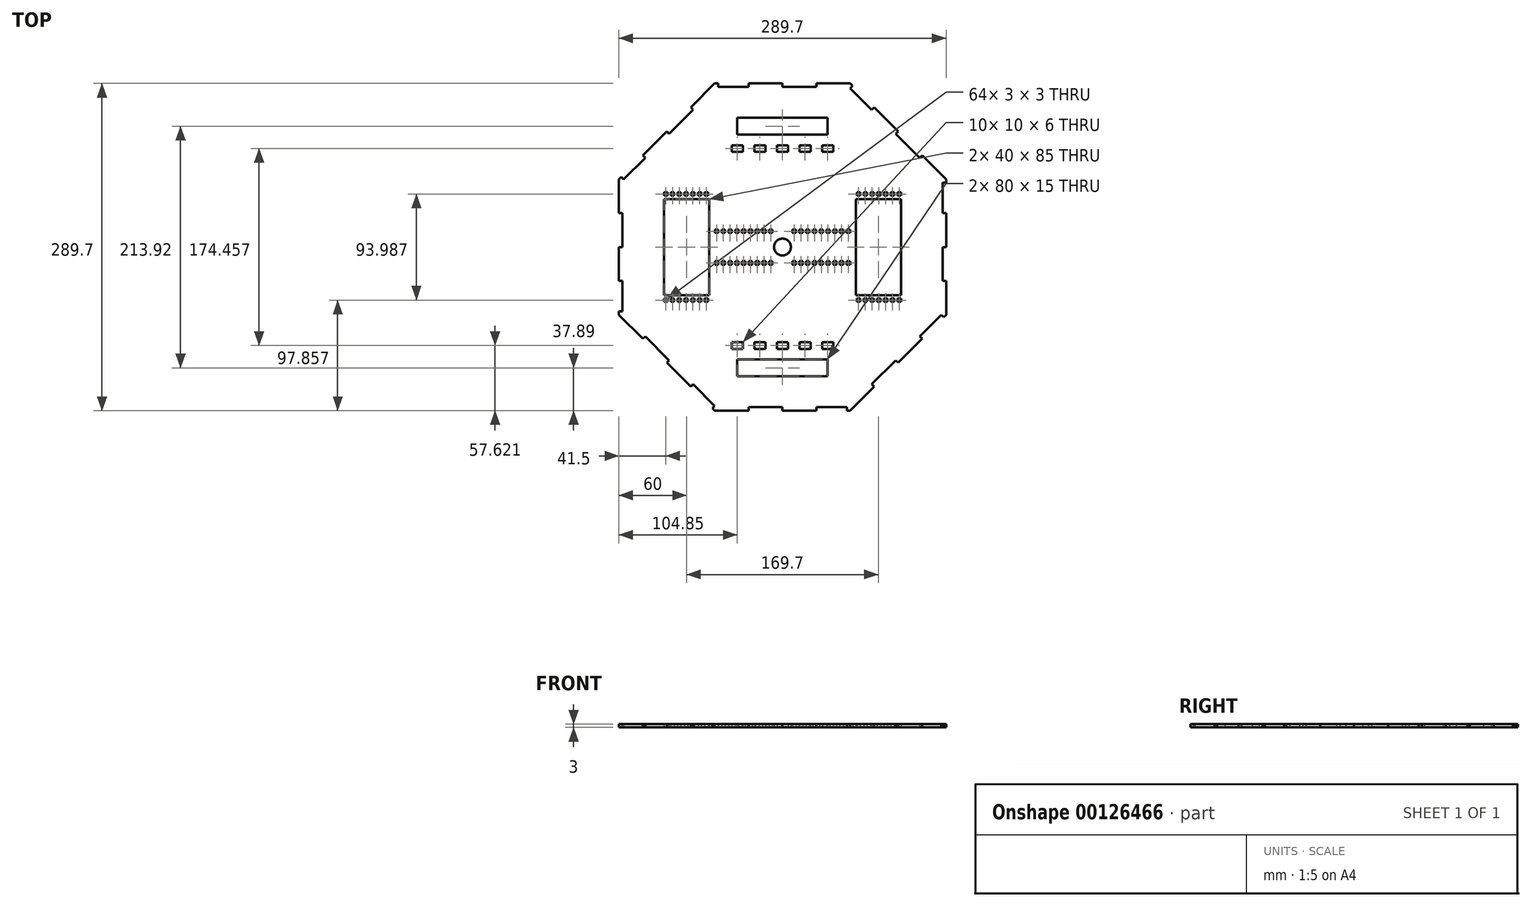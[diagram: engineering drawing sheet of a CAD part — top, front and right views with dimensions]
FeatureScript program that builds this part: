
annotation { "Feature Type Name" : "Feature", "Feature Type Description" : "" }
export const myFeature = defineFeature(function(context is Context, id is Id, definition is map)
    precondition{}
    {
        {
            var Q0;
            Q0=qCreatedBy(makeId("Top.planeOp"),FACE);
            var sketch = newSketch(context, id + "F0", { "sketchPlane" : qUnion([Q0])});
            skArc(sketch, "E0.cCircle", {"start": v(0, -144.85) * mm, "mid": v(14.74, 144.1) * mm, "end": v(-29.33, -141.85) * mm, "construction": true});
            skLineSegment(sketch, "E0.0", {"start": v(-60, 144.85) * mm, "end": v(-57, 144.85) * mm});
            skLineSegment(sketch, "E0.1", {"start": v(60, 144.85) * mm, "end": v(62.12, 142.73) * mm});
            skLineSegment(sketch, "E0.2", {"start": v(144.85, 60) * mm, "end": v(144.85, 57) * mm});
            skLineSegment(sketch, "E0.3", {"start": v(144.85, -60) * mm, "end": v(142.73, -62.12) * mm});
            skLineSegment(sketch, "E0.4", {"start": v(60, -144.85) * mm, "end": v(57, -144.85) * mm});
            skLineSegment(sketch, "E0.5", {"start": v(-60, -144.85) * mm, "end": v(-62.12, -142.73) * mm});
            skLineSegment(sketch, "E0.6", {"start": v(-144.85, -60) * mm, "end": v(-144.85, -57) * mm});
            skLineSegment(sketch, "E0.7", {"start": v(-144.85, 60) * mm, "end": v(-142.73, 62.12) * mm});
            skPoint(sketch, "E0.0.midPoint", {"position": v(0, 144.85) * mm});
            skLineSegment(sketch, "E1", {"start": v(144.85, 0) * mm, "end": v(-144.85, 0) * mm, "construction": true});
            skLineSegment(sketch, "E2", {"start": v(-144.85, 0) * mm, "end": v(-104.85, 0) * mm, "construction": true});
            skLineSegment(sketch, "E3", {"start": v(-104.85, 0) * mm, "end": v(-104.85, 42.5) * mm});
            skLineSegment(sketch, "E4", {"start": v(-104.85, 42.5) * mm, "end": v(-64.85, 42.5) * mm});
            skLineSegment(sketch, "E5", {"start": v(-64.85, 42.5) * mm, "end": v(-64.85, -42.5) * mm});
            skLineSegment(sketch, "E6", {"start": v(-64.85, -42.5) * mm, "end": v(-104.85, -42.5) * mm});
            skLineSegment(sketch, "E7", {"start": v(-104.85, -42.5) * mm, "end": v(-104.85, 0) * mm});
            skLineSegment(sketch, "E8", {"start": v(-64.85, 0) * mm, "end": v(-59.85, 0) * mm, "construction": true});
            skLineSegment(sketch, "E9", {"start": v(-59.85, 0) * mm, "end": v(-59.85, 15.5) * mm, "construction": true});
            skLineSegment(sketch, "E10", {"start": v(-59.85, 0) * mm, "end": v(-56.85, 0) * mm, "construction": true});
            skLineSegment(sketch, "E11", {"start": v(-56.85, 0) * mm, "end": v(-53.85, 0) * mm, "construction": true});
            skLineSegment(sketch, "E12", {"start": v(-53.85, 0) * mm, "end": v(-50.85, 0) * mm, "construction": true});
            skLineSegment(sketch, "E13", {"start": v(-50.85, 0) * mm, "end": v(-47.85, 0) * mm, "construction": true});
            skLineSegment(sketch, "E14", {"start": v(-47.85, 0) * mm, "end": v(-44.85, 0) * mm, "construction": true});
            skLineSegment(sketch, "E15", {"start": v(-44.85, 0) * mm, "end": v(-41.85, 0) * mm, "construction": true});
            skLineSegment(sketch, "E16", {"start": v(-41.85, 0) * mm, "end": v(-38.85, 0) * mm, "construction": true});
            skLineSegment(sketch, "E17", {"start": v(-38.85, 0) * mm, "end": v(-35.85, 0) * mm, "construction": true});
            skLineSegment(sketch, "E18", {"start": v(-35.85, 0) * mm, "end": v(-32.85, 0) * mm, "construction": true});
            skLineSegment(sketch, "E19", {"start": v(-32.85, 0) * mm, "end": v(-29.85, 0) * mm, "construction": true});
            skLineSegment(sketch, "E20", {"start": v(-29.85, 0) * mm, "end": v(-26.85, 0) * mm, "construction": true});
            skLineSegment(sketch, "E21", {"start": v(-26.85, 0) * mm, "end": v(-23.85, 0) * mm, "construction": true});
            skLineSegment(sketch, "E22", {"start": v(-23.85, 0) * mm, "end": v(-20.85, 0) * mm, "construction": true});
            skLineSegment(sketch, "E23", {"start": v(-20.85, 0) * mm, "end": v(-17.85, 0) * mm, "construction": true});
            skLineSegment(sketch, "E24", {"start": v(-17.85, 0) * mm, "end": v(-14.85, 0) * mm, "construction": true});
            skLineSegment(sketch, "E25", {"start": v(-14.85, 0) * mm, "end": v(-11.85, 0) * mm, "construction": true});
            skLineSegment(sketch, "E26", {"start": v(-59.85, 15.5) * mm, "end": v(-56.85, 15.5) * mm});
            skLineSegment(sketch, "E27", {"start": v(-56.85, 15.5) * mm, "end": v(-56.85, 12.5) * mm});
            skLineSegment(sketch, "E28", {"start": v(-56.85, 12.5) * mm, "end": v(-59.85, 12.5) * mm});
            skLineSegment(sketch, "E29", {"start": v(-59.85, 12.5) * mm, "end": v(-59.85, 15.5) * mm});
            skLineSegment(sketch, "E30", {"start": v(-53.85, 15.5) * mm, "end": v(-50.85, 15.5) * mm});
            skLineSegment(sketch, "E31", {"start": v(-50.85, 15.5) * mm, "end": v(-50.85, 12.5) * mm});
            skLineSegment(sketch, "E32", {"start": v(-50.85, 12.5) * mm, "end": v(-53.85, 12.5) * mm});
            skLineSegment(sketch, "E33", {"start": v(-59.85, 15.5) * mm, "end": v(-11.85, 15.5) * mm, "construction": true});
            skLineSegment(sketch, "E34", {"start": v(-47.85, 0) * mm, "end": v(-47.85, 15.5) * mm, "construction": true});
            skLineSegment(sketch, "E35", {"start": v(-41.85, 0) * mm, "end": v(-41.85, 15.5) * mm, "construction": true});
            skLineSegment(sketch, "E36", {"start": v(-35.85, 0) * mm, "end": v(-35.85, 15.5) * mm, "construction": true});
            skLineSegment(sketch, "E37", {"start": v(-29.85, 0) * mm, "end": v(-29.85, 15.5) * mm, "construction": true});
            skLineSegment(sketch, "E38", {"start": v(-23.85, 0) * mm, "end": v(-23.85, 15.5) * mm, "construction": true});
            skLineSegment(sketch, "E39", {"start": v(-17.85, 0) * mm, "end": v(-17.85, 15.5) * mm, "construction": true});
            skLineSegment(sketch, "E40", {"start": v(-53.85, 15.5) * mm, "end": v(-53.85, 12.5) * mm});
            skLineSegment(sketch, "E41", {"start": v(-47.85, 15.5) * mm, "end": v(-47.85, 12.5) * mm});
            skLineSegment(sketch, "E42", {"start": v(-47.85, 12.5) * mm, "end": v(-44.85, 12.5) * mm});
            skLineSegment(sketch, "E43", {"start": v(-44.85, 12.5) * mm, "end": v(-44.85, 15.5) * mm});
            skLineSegment(sketch, "E44", {"start": v(-44.85, 15.5) * mm, "end": v(-47.85, 15.5) * mm});
            skLineSegment(sketch, "E45", {"start": v(-41.85, 15.5) * mm, "end": v(-41.85, 12.5) * mm});
            skLineSegment(sketch, "E46", {"start": v(-41.85, 12.5) * mm, "end": v(-38.85, 12.5) * mm});
            skLineSegment(sketch, "E47", {"start": v(-38.85, 12.5) * mm, "end": v(-38.85, 15.5) * mm});
            skLineSegment(sketch, "E48", {"start": v(-38.85, 15.5) * mm, "end": v(-41.85, 15.5) * mm});
            skLineSegment(sketch, "E49", {"start": v(-35.85, 15.5) * mm, "end": v(-35.85, 12.5) * mm});
            skLineSegment(sketch, "E50", {"start": v(-35.85, 12.5) * mm, "end": v(-32.85, 12.5) * mm});
            skLineSegment(sketch, "E51", {"start": v(-32.85, 12.5) * mm, "end": v(-32.85, 15.5) * mm});
            skLineSegment(sketch, "E52", {"start": v(-32.85, 15.5) * mm, "end": v(-35.85, 15.5) * mm});
            skLineSegment(sketch, "E53", {"start": v(-29.85, 15.5) * mm, "end": v(-29.85, 12.5) * mm});
            skLineSegment(sketch, "E54", {"start": v(-29.85, 12.5) * mm, "end": v(-26.85, 12.5) * mm});
            skLineSegment(sketch, "E55", {"start": v(-26.85, 12.5) * mm, "end": v(-26.85, 15.5) * mm});
            skLineSegment(sketch, "E56", {"start": v(-26.85, 15.5) * mm, "end": v(-29.85, 15.5) * mm});
            skLineSegment(sketch, "E57", {"start": v(-23.85, 15.5) * mm, "end": v(-23.85, 12.5) * mm});
            skLineSegment(sketch, "E58", {"start": v(-23.85, 12.5) * mm, "end": v(-20.85, 12.5) * mm});
            skLineSegment(sketch, "E59", {"start": v(-20.85, 12.5) * mm, "end": v(-20.85, 15.5) * mm});
            skLineSegment(sketch, "E60", {"start": v(-20.85, 15.5) * mm, "end": v(-23.85, 15.5) * mm});
            skLineSegment(sketch, "E61", {"start": v(-17.85, 15.5) * mm, "end": v(-17.85, 12.5) * mm});
            skLineSegment(sketch, "E62", {"start": v(-17.85, 12.5) * mm, "end": v(-14.85, 12.5) * mm});
            skLineSegment(sketch, "E63", {"start": v(-14.85, 12.5) * mm, "end": v(-14.85, 15.5) * mm});
            skLineSegment(sketch, "E64", {"start": v(-14.85, 15.5) * mm, "end": v(-17.85, 15.5) * mm});
            skLineSegment(sketch, "E65", {"start": v(-11.85, 15.5) * mm, "end": v(-11.85, 12.5) * mm});
            skLineSegment(sketch, "E66", {"start": v(-11.85, 12.5) * mm, "end": v(-8.85, 12.5) * mm});
            skLineSegment(sketch, "E67", {"start": v(-8.85, 12.5) * mm, "end": v(-8.85, 15.5) * mm});
            skLineSegment(sketch, "E68", {"start": v(-8.85, 15.5) * mm, "end": v(-11.85, 15.5) * mm});
            skLineSegment(sketch, "E69.MirrorCS", {"start": v(-47.85, -15.5) * mm, "end": v(-47.85, -12.5) * mm});
            skLineSegment(sketch, "E70.MirrorCS", {"start": v(-50.85, -12.5) * mm, "end": v(-53.85, -12.5) * mm});
            skLineSegment(sketch, "E71.MirrorCS", {"start": v(-53.85, -15.5) * mm, "end": v(-53.85, -12.5) * mm});
            skLineSegment(sketch, "E72.MirrorCS", {"start": v(-50.85, -15.5) * mm, "end": v(-50.85, -12.5) * mm});
            skLineSegment(sketch, "E73.MirrorCS", {"start": v(-41.85, -15.5) * mm, "end": v(-41.85, -12.5) * mm});
            skLineSegment(sketch, "E74.MirrorCS", {"start": v(-47.85, -12.5) * mm, "end": v(-44.85, -12.5) * mm});
            skLineSegment(sketch, "E75.MirrorCS", {"start": v(-59.85, -15.5) * mm, "end": v(-56.85, -15.5) * mm});
            skLineSegment(sketch, "E76.MirrorCS", {"start": v(-44.85, -12.5) * mm, "end": v(-44.85, -15.5) * mm});
            skLineSegment(sketch, "E77.MirrorCS", {"start": v(-32.85, -15.5) * mm, "end": v(-35.85, -15.5) * mm});
            skLineSegment(sketch, "E78.MirrorCS", {"start": v(-41.85, -12.5) * mm, "end": v(-38.85, -12.5) * mm});
            skLineSegment(sketch, "E79.MirrorCS", {"start": v(-53.85, -15.5) * mm, "end": v(-50.85, -15.5) * mm});
            skLineSegment(sketch, "E80.MirrorCS", {"start": v(-23.85, -15.5) * mm, "end": v(-23.85, -12.5) * mm});
            skLineSegment(sketch, "E81.MirrorCS", {"start": v(-14.85, -15.5) * mm, "end": v(-17.85, -15.5) * mm});
            skLineSegment(sketch, "E82.MirrorCS", {"start": v(-38.85, -15.5) * mm, "end": v(-41.85, -15.5) * mm});
            skLineSegment(sketch, "E83.MirrorCS", {"start": v(-35.85, -15.5) * mm, "end": v(-35.85, -12.5) * mm});
            skLineSegment(sketch, "E84.MirrorCS", {"start": v(-59.85, -15.5) * mm, "end": v(-11.85, -15.5) * mm, "construction": true});
            skLineSegment(sketch, "E85.MirrorCS", {"start": v(-26.85, -15.5) * mm, "end": v(-29.85, -15.5) * mm});
            skLineSegment(sketch, "E86.MirrorCS", {"start": v(-11.85, -15.5) * mm, "end": v(-11.85, -12.5) * mm});
            skLineSegment(sketch, "E87.MirrorCS", {"start": v(-14.85, -12.5) * mm, "end": v(-14.85, -15.5) * mm});
            skLineSegment(sketch, "E88.MirrorCS", {"start": v(-38.85, -12.5) * mm, "end": v(-38.85, -15.5) * mm});
            skLineSegment(sketch, "E89.MirrorCS", {"start": v(-29.85, -12.5) * mm, "end": v(-26.85, -12.5) * mm});
            skLineSegment(sketch, "E90.MirrorCS", {"start": v(-23.85, -12.5) * mm, "end": v(-20.85, -12.5) * mm});
            skLineSegment(sketch, "E91.MirrorCS", {"start": v(-56.85, -12.5) * mm, "end": v(-59.85, -12.5) * mm});
            skLineSegment(sketch, "E92.MirrorCS", {"start": v(-17.85, -15.5) * mm, "end": v(-17.85, -12.5) * mm});
            skLineSegment(sketch, "E93.MirrorCS", {"start": v(-44.85, -15.5) * mm, "end": v(-47.85, -15.5) * mm});
            skLineSegment(sketch, "E94.MirrorCS", {"start": v(-59.85, -12.5) * mm, "end": v(-59.85, -15.5) * mm});
            skLineSegment(sketch, "E95.MirrorCS", {"start": v(-8.85, -15.5) * mm, "end": v(-11.85, -15.5) * mm});
            skLineSegment(sketch, "E96.MirrorCS", {"start": v(-20.85, -12.5) * mm, "end": v(-20.85, -15.5) * mm});
            skLineSegment(sketch, "E97.MirrorCS", {"start": v(-56.85, -15.5) * mm, "end": v(-56.85, -12.5) * mm});
            skLineSegment(sketch, "E98.MirrorCS", {"start": v(-17.85, -12.5) * mm, "end": v(-14.85, -12.5) * mm});
            skLineSegment(sketch, "E99.MirrorCS", {"start": v(-32.85, -12.5) * mm, "end": v(-32.85, -15.5) * mm});
            skLineSegment(sketch, "E100.MirrorCS", {"start": v(-26.85, -12.5) * mm, "end": v(-26.85, -15.5) * mm});
            skLineSegment(sketch, "E101.MirrorCS", {"start": v(-8.85, -12.5) * mm, "end": v(-8.85, -15.5) * mm});
            skLineSegment(sketch, "E102.MirrorCS", {"start": v(-11.85, -12.5) * mm, "end": v(-8.85, -12.5) * mm});
            skLineSegment(sketch, "E103.MirrorCS", {"start": v(-35.85, -12.5) * mm, "end": v(-32.85, -12.5) * mm});
            skLineSegment(sketch, "E104.MirrorCS", {"start": v(-20.85, -15.5) * mm, "end": v(-23.85, -15.5) * mm});
            skLineSegment(sketch, "E105.MirrorCS", {"start": v(-29.85, -15.5) * mm, "end": v(-29.85, -12.5) * mm});
            skLineSegment(sketch, "E106.MirrorCS", {"start": v(-59.85, 0) * mm, "end": v(-59.85, -15.5) * mm, "construction": true});
            skLineSegment(sketch, "E107.MirrorCS", {"start": v(-17.85, 0) * mm, "end": v(-17.85, -15.5) * mm, "construction": true});
            skLineSegment(sketch, "E108.MirrorCS", {"start": v(-29.85, 0) * mm, "end": v(-29.85, -15.5) * mm, "construction": true});
            skLineSegment(sketch, "E109.MirrorCS", {"start": v(-23.85, 0) * mm, "end": v(-23.85, -15.5) * mm, "construction": true});
            skLineSegment(sketch, "E110.MirrorCS", {"start": v(-35.85, 0) * mm, "end": v(-35.85, -15.5) * mm, "construction": true});
            skLineSegment(sketch, "E111.MirrorCS", {"start": v(-41.85, 0) * mm, "end": v(-41.85, -15.5) * mm, "construction": true});
            skLineSegment(sketch, "E112.MirrorCS", {"start": v(-47.85, 0) * mm, "end": v(-47.85, -15.5) * mm, "construction": true});
            skLineSegment(sketch, "E113.MirrorCS", {"start": v(26.85, 12.5) * mm, "end": v(26.85, 15.5) * mm});
            skLineSegment(sketch, "E114.MirrorCS", {"start": v(23.85, 12.5) * mm, "end": v(20.85, 12.5) * mm});
            skLineSegment(sketch, "E115.MirrorCS", {"start": v(26.85, 15.5) * mm, "end": v(29.85, 15.5) * mm});
            skLineSegment(sketch, "E116.MirrorCS", {"start": v(20.85, 12.5) * mm, "end": v(20.85, 15.5) * mm});
            skLineSegment(sketch, "E117.MirrorCS", {"start": v(23.85, 15.5) * mm, "end": v(23.85, 12.5) * mm});
            skLineSegment(sketch, "E118.MirrorCS", {"start": v(20.85, 15.5) * mm, "end": v(23.85, 15.5) * mm});
            skLineSegment(sketch, "E119.MirrorCS", {"start": v(17.85, 15.5) * mm, "end": v(17.85, 12.5) * mm});
            skLineSegment(sketch, "E120.MirrorCS", {"start": v(32.85, 15.5) * mm, "end": v(35.85, 15.5) * mm});
            skLineSegment(sketch, "E121.MirrorCS", {"start": v(35.85, 15.5) * mm, "end": v(35.85, 12.5) * mm});
            skLineSegment(sketch, "E122.MirrorCS", {"start": v(38.85, 0) * mm, "end": v(35.85, 0) * mm, "construction": true});
            skLineSegment(sketch, "E123.MirrorCS", {"start": v(32.85, 12.5) * mm, "end": v(32.85, 15.5) * mm});
            skLineSegment(sketch, "E124.MirrorCS", {"start": v(32.85, 0) * mm, "end": v(29.85, 0) * mm, "construction": true});
            skLineSegment(sketch, "E125.MirrorCS", {"start": v(35.85, 0) * mm, "end": v(32.85, 0) * mm, "construction": true});
            skLineSegment(sketch, "E126.MirrorCS", {"start": v(29.85, 12.5) * mm, "end": v(26.85, 12.5) * mm});
            skLineSegment(sketch, "E127.MirrorCS", {"start": v(29.85, 15.5) * mm, "end": v(29.85, 12.5) * mm});
            skLineSegment(sketch, "E128.MirrorCS", {"start": v(35.85, 12.5) * mm, "end": v(32.85, 12.5) * mm});
            skLineSegment(sketch, "E129.MirrorCS", {"start": v(47.85, 12.5) * mm, "end": v(44.85, 12.5) * mm});
            skLineSegment(sketch, "E130.MirrorCS", {"start": v(44.85, 12.5) * mm, "end": v(44.85, 15.5) * mm});
            skLineSegment(sketch, "E131.MirrorCS", {"start": v(47.85, 15.5) * mm, "end": v(47.85, 12.5) * mm});
            skLineSegment(sketch, "E132.MirrorCS", {"start": v(44.85, 15.5) * mm, "end": v(47.85, 15.5) * mm});
            skLineSegment(sketch, "E133.MirrorCS", {"start": v(41.85, 15.5) * mm, "end": v(41.85, 12.5) * mm});
            skLineSegment(sketch, "E134.MirrorCS", {"start": v(41.85, 12.5) * mm, "end": v(38.85, 12.5) * mm});
            skLineSegment(sketch, "E135.MirrorCS", {"start": v(53.85, 15.5) * mm, "end": v(50.85, 15.5) * mm});
            skLineSegment(sketch, "E136.MirrorCS", {"start": v(41.85, -12.5) * mm, "end": v(38.85, -12.5) * mm});
            skLineSegment(sketch, "E137.MirrorCS", {"start": v(17.85, 12.5) * mm, "end": v(14.85, 12.5) * mm});
            skLineSegment(sketch, "E138.MirrorCS", {"start": v(38.85, 12.5) * mm, "end": v(38.85, 15.5) * mm});
            skLineSegment(sketch, "E139.MirrorCS", {"start": v(50.85, 15.5) * mm, "end": v(50.85, 12.5) * mm});
            skLineSegment(sketch, "E140.MirrorCS", {"start": v(38.85, 15.5) * mm, "end": v(41.85, 15.5) * mm});
            skLineSegment(sketch, "E141.MirrorCS", {"start": v(50.85, 12.5) * mm, "end": v(53.85, 12.5) * mm});
            skLineSegment(sketch, "E142.MirrorCS", {"start": v(29.85, 0) * mm, "end": v(26.85, 0) * mm, "construction": true});
            skLineSegment(sketch, "E143.MirrorCS", {"start": v(35.85, 0) * mm, "end": v(35.85, 15.5) * mm, "construction": true});
            skLineSegment(sketch, "E144.MirrorCS", {"start": v(38.85, -15.5) * mm, "end": v(41.85, -15.5) * mm});
            skLineSegment(sketch, "E145.MirrorCS", {"start": v(29.85, 0) * mm, "end": v(29.85, 15.5) * mm, "construction": true});
            skLineSegment(sketch, "E146.MirrorCS", {"start": v(26.85, 0) * mm, "end": v(23.85, 0) * mm, "construction": true});
            skLineSegment(sketch, "E147.MirrorCS", {"start": v(47.85, -12.5) * mm, "end": v(44.85, -12.5) * mm});
            skLineSegment(sketch, "E148.MirrorCS", {"start": v(59.85, 15.5) * mm, "end": v(56.85, 15.5) * mm});
            skLineSegment(sketch, "E149.MirrorCS", {"start": v(23.85, -12.5) * mm, "end": v(20.85, -12.5) * mm});
            skLineSegment(sketch, "E150.MirrorCS", {"start": v(38.85, -12.5) * mm, "end": v(38.85, -15.5) * mm});
            skLineSegment(sketch, "E151.MirrorCS", {"start": v(41.85, -15.5) * mm, "end": v(41.85, -12.5) * mm});
            skLineSegment(sketch, "E152.MirrorCS", {"start": v(53.85, 0) * mm, "end": v(50.85, 0) * mm, "construction": true});
            skLineSegment(sketch, "E153.MirrorCS", {"start": v(17.85, -15.5) * mm, "end": v(17.85, -12.5) * mm});
            skLineSegment(sketch, "E154.MirrorCS", {"start": v(50.85, 0) * mm, "end": v(47.85, 0) * mm, "construction": true});
            skLineSegment(sketch, "E155.MirrorCS", {"start": v(32.85, -15.5) * mm, "end": v(35.85, -15.5) * mm});
            skLineSegment(sketch, "E156.MirrorCS", {"start": v(47.85, 0) * mm, "end": v(44.85, 0) * mm, "construction": true});
            skLineSegment(sketch, "E157.MirrorCS", {"start": v(44.85, 0) * mm, "end": v(41.85, 0) * mm, "construction": true});
            skLineSegment(sketch, "E158.MirrorCS", {"start": v(14.85, 12.5) * mm, "end": v(14.85, 15.5) * mm});
            skLineSegment(sketch, "E159.MirrorCS", {"start": v(41.85, 0) * mm, "end": v(38.85, 0) * mm, "construction": true});
            skLineSegment(sketch, "E160.MirrorCS", {"start": v(20.85, -12.5) * mm, "end": v(20.85, -15.5) * mm});
            skLineSegment(sketch, "E161.MirrorCS", {"start": v(14.85, 15.5) * mm, "end": v(17.85, 15.5) * mm});
            skLineSegment(sketch, "E162.MirrorCS", {"start": v(14.85, -12.5) * mm, "end": v(14.85, -15.5) * mm});
            skLineSegment(sketch, "E163.MirrorCS", {"start": v(17.85, -12.5) * mm, "end": v(14.85, -12.5) * mm});
            skLineSegment(sketch, "E164.MirrorCS", {"start": v(14.85, -15.5) * mm, "end": v(17.85, -15.5) * mm});
            skLineSegment(sketch, "E165.MirrorCS", {"start": v(11.85, 15.5) * mm, "end": v(11.85, 12.5) * mm});
            skLineSegment(sketch, "E166.MirrorCS", {"start": v(35.85, -15.5) * mm, "end": v(35.85, -12.5) * mm});
            skLineSegment(sketch, "E167.MirrorCS", {"start": v(47.85, 0) * mm, "end": v(47.85, 15.5) * mm, "construction": true});
            skLineSegment(sketch, "E168.MirrorCS", {"start": v(17.85, 0) * mm, "end": v(17.85, 15.5) * mm, "construction": true});
            skLineSegment(sketch, "E169.MirrorCS", {"start": v(20.85, 0) * mm, "end": v(17.85, 0) * mm, "construction": true});
            skLineSegment(sketch, "E170.MirrorCS", {"start": v(59.85, 0) * mm, "end": v(56.85, 0) * mm, "construction": true});
            skLineSegment(sketch, "E171.MirrorCS", {"start": v(64.85, 0) * mm, "end": v(59.85, 0) * mm, "construction": true});
            skLineSegment(sketch, "E172.MirrorCS", {"start": v(53.85, 15.5) * mm, "end": v(53.85, 12.5) * mm});
            skLineSegment(sketch, "E173.MirrorCS", {"start": v(17.85, 0) * mm, "end": v(14.85, 0) * mm, "construction": true});
            skLineSegment(sketch, "E174.MirrorCS", {"start": v(20.85, -15.5) * mm, "end": v(23.85, -15.5) * mm});
            skLineSegment(sketch, "E175.MirrorCS", {"start": v(56.85, 0) * mm, "end": v(53.85, 0) * mm, "construction": true});
            skLineSegment(sketch, "E176.MirrorCS", {"start": v(59.85, -15.5) * mm, "end": v(56.85, -15.5) * mm});
            skLineSegment(sketch, "E177.MirrorCS", {"start": v(56.85, 15.5) * mm, "end": v(56.85, 12.5) * mm});
            skLineSegment(sketch, "E178.MirrorCS", {"start": v(56.85, -12.5) * mm, "end": v(59.85, -12.5) * mm});
            skLineSegment(sketch, "E179.MirrorCS", {"start": v(59.85, 0) * mm, "end": v(59.85, 15.5) * mm, "construction": true});
            skLineSegment(sketch, "E180.MirrorCS", {"start": v(14.85, 0) * mm, "end": v(11.85, 0) * mm, "construction": true});
            skLineSegment(sketch, "E181.MirrorCS", {"start": v(29.85, -15.5) * mm, "end": v(29.85, -12.5) * mm});
            skLineSegment(sketch, "E182.MirrorCS", {"start": v(29.85, -12.5) * mm, "end": v(26.85, -12.5) * mm});
            skLineSegment(sketch, "E183.MirrorCS", {"start": v(44.85, -12.5) * mm, "end": v(44.85, -15.5) * mm});
            skLineSegment(sketch, "E184.MirrorCS", {"start": v(56.85, 12.5) * mm, "end": v(59.85, 12.5) * mm});
            skLineSegment(sketch, "E185.MirrorCS", {"start": v(59.85, 12.5) * mm, "end": v(59.85, 15.5) * mm});
            skLineSegment(sketch, "E186.MirrorCS", {"start": v(44.85, -15.5) * mm, "end": v(47.85, -15.5) * mm});
            skLineSegment(sketch, "E187.MirrorCS", {"start": v(53.85, -15.5) * mm, "end": v(50.85, -15.5) * mm});
            skLineSegment(sketch, "E188.MirrorCS", {"start": v(23.85, -15.5) * mm, "end": v(23.85, -12.5) * mm});
            skLineSegment(sketch, "E189.MirrorCS", {"start": v(26.85, -12.5) * mm, "end": v(26.85, -15.5) * mm});
            skLineSegment(sketch, "E190.MirrorCS", {"start": v(35.85, -12.5) * mm, "end": v(32.85, -12.5) * mm});
            skLineSegment(sketch, "E191.MirrorCS", {"start": v(8.85, 15.5) * mm, "end": v(11.85, 15.5) * mm});
            skLineSegment(sketch, "E192.MirrorCS", {"start": v(11.85, 12.5) * mm, "end": v(8.85, 12.5) * mm});
            skLineSegment(sketch, "E193.MirrorCS", {"start": v(59.85, 15.5) * mm, "end": v(11.85, 15.5) * mm, "construction": true});
            skLineSegment(sketch, "E194.MirrorCS", {"start": v(41.85, 0) * mm, "end": v(41.85, 15.5) * mm, "construction": true});
            skLineSegment(sketch, "E195.MirrorCS", {"start": v(32.85, -12.5) * mm, "end": v(32.85, -15.5) * mm});
            skLineSegment(sketch, "E196.MirrorCS", {"start": v(8.85, 12.5) * mm, "end": v(8.85, 15.5) * mm});
            skLineSegment(sketch, "E197.MirrorCS", {"start": v(47.85, -15.5) * mm, "end": v(47.85, -12.5) * mm});
            skLineSegment(sketch, "E198.MirrorCS", {"start": v(50.85, -12.5) * mm, "end": v(53.85, -12.5) * mm});
            skLineSegment(sketch, "E199.MirrorCS", {"start": v(23.85, 0) * mm, "end": v(23.85, 15.5) * mm, "construction": true});
            skLineSegment(sketch, "E200.MirrorCS", {"start": v(26.85, -15.5) * mm, "end": v(29.85, -15.5) * mm});
            skLineSegment(sketch, "E201.MirrorCS", {"start": v(23.85, 0) * mm, "end": v(20.85, 0) * mm, "construction": true});
            skLineSegment(sketch, "E202.MirrorCS", {"start": v(53.85, -15.5) * mm, "end": v(53.85, -12.5) * mm});
            skLineSegment(sketch, "E203.MirrorCS", {"start": v(50.85, -15.5) * mm, "end": v(50.85, -12.5) * mm});
            skLineSegment(sketch, "E204.MirrorCS", {"start": v(59.85, -12.5) * mm, "end": v(59.85, -15.5) * mm});
            skLineSegment(sketch, "E205.MirrorCS", {"start": v(59.85, -15.5) * mm, "end": v(11.85, -15.5) * mm, "construction": true});
            skLineSegment(sketch, "E206.MirrorCS", {"start": v(56.85, -15.5) * mm, "end": v(56.85, -12.5) * mm});
            skLineSegment(sketch, "E207.MirrorCS", {"start": v(8.85, -15.5) * mm, "end": v(11.85, -15.5) * mm});
            skLineSegment(sketch, "E208.MirrorCS", {"start": v(11.85, -12.5) * mm, "end": v(8.85, -12.5) * mm});
            skLineSegment(sketch, "E209.MirrorCS", {"start": v(11.85, -15.5) * mm, "end": v(11.85, -12.5) * mm});
            skLineSegment(sketch, "E210.MirrorCS", {"start": v(8.85, -12.5) * mm, "end": v(8.85, -15.5) * mm});
            skLineSegment(sketch, "E211.MirrorCS", {"start": v(104.85, -42.5) * mm, "end": v(104.85, 0) * mm});
            skLineSegment(sketch, "E212.MirrorCS", {"start": v(59.85, 0) * mm, "end": v(59.85, -15.5) * mm, "construction": true});
            skLineSegment(sketch, "E213.MirrorCS", {"start": v(17.85, 0) * mm, "end": v(17.85, -15.5) * mm, "construction": true});
            skLineSegment(sketch, "E214.MirrorCS", {"start": v(29.85, 0) * mm, "end": v(29.85, -15.5) * mm, "construction": true});
            skLineSegment(sketch, "E215.MirrorCS", {"start": v(23.85, 0) * mm, "end": v(23.85, -15.5) * mm, "construction": true});
            skLineSegment(sketch, "E216.MirrorCS", {"start": v(35.85, 0) * mm, "end": v(35.85, -15.5) * mm, "construction": true});
            skLineSegment(sketch, "E217.MirrorCS", {"start": v(41.85, 0) * mm, "end": v(41.85, -15.5) * mm, "construction": true});
            skLineSegment(sketch, "E218.MirrorCS", {"start": v(47.85, 0) * mm, "end": v(47.85, -15.5) * mm, "construction": true});
            skLineSegment(sketch, "E219.MirrorCS", {"start": v(104.85, 0) * mm, "end": v(104.85, 42.5) * mm});
            skLineSegment(sketch, "E220.MirrorCS", {"start": v(64.85, -42.5) * mm, "end": v(104.85, -42.5) * mm});
            skLineSegment(sketch, "E221.MirrorCS", {"start": v(64.85, 42.5) * mm, "end": v(64.85, -42.5) * mm});
            skLineSegment(sketch, "E222.MirrorCS", {"start": v(104.85, 42.5) * mm, "end": v(64.85, 42.5) * mm});
            skCircle(sketch, "E223.MirrorC", {"center": v(0, 0) * mm, "radius": 144.85 * mm, "construction": true});
            skLineSegment(sketch, "E224", {"start": v(-60, -144.85) * mm, "end": v(-30, -144.85) * mm});
            skLineSegment(sketch, "E225", {"start": v(-30, -144.85) * mm, "end": v(-30, -141.85) * mm});
            skLineSegment(sketch, "E226", {"start": v(-30, -141.85) * mm, "end": v(0, -141.85) * mm});
            skLineSegment(sketch, "E227", {"start": v(0, -141.85) * mm, "end": v(0, -144.85) * mm});
            skLineSegment(sketch, "E228", {"start": v(0, -144.85) * mm, "end": v(30, -144.85) * mm});
            skLineSegment(sketch, "E229", {"start": v(30, -144.85) * mm, "end": v(30, -141.85) * mm});
            skLineSegment(sketch, "E230", {"start": v(60, -144.85) * mm, "end": v(0, -84.85) * mm, "construction": true});
            skLineSegment(sketch, "E231", {"start": v(0, -84.85) * mm, "end": v(-60, -144.85) * mm, "construction": true});
            skLineSegment(sketch, "E232", {"start": v(30, -141.85) * mm, "end": v(57, -141.85) * mm});
            skLineSegment(sketch, "E233", {"start": v(57, -141.85) * mm, "end": v(57, -144.85) * mm});
            skLineSegment(sketch, "E234.trimOffspring", {"start": v(-30, -144.85) * mm, "end": v(-60, -144.85) * mm});
            skLineSegment(sketch, "E235.trimOffspring", {"start": v(30, -144.85) * mm, "end": v(0, -144.85) * mm});
            skLineSegment(sketch, "E236", {"start": v(60, -144.85) * mm, "end": v(81.21, -123.64) * mm});
            skLineSegment(sketch, "E237", {"start": v(81.21, -123.64) * mm, "end": v(79.1, -121.52) * mm});
            skLineSegment(sketch, "E238", {"start": v(79.1, -121.52) * mm, "end": v(100.3, -100.3) * mm});
            skLineSegment(sketch, "E239", {"start": v(100.3, -100.3) * mm, "end": v(102.43, -102.42) * mm});
            skLineSegment(sketch, "E240", {"start": v(102.43, -102.42) * mm, "end": v(123.64, -81.21) * mm});
            skLineSegment(sketch, "E241", {"start": v(123.64, -81.21) * mm, "end": v(121.52, -79.09) * mm});
            skLineSegment(sketch, "E242", {"start": v(121.52, -79.09) * mm, "end": v(140.6, -60) * mm});
            skLineSegment(sketch, "E243", {"start": v(140.6, -60) * mm, "end": v(142.73, -62.12) * mm});
            skLineSegment(sketch, "E244", {"start": v(144.85, -60) * mm, "end": v(144.85, -30) * mm});
            skLineSegment(sketch, "E245", {"start": v(144.85, -30) * mm, "end": v(141.85, -30) * mm});
            skLineSegment(sketch, "E246", {"start": v(141.85, -30) * mm, "end": v(141.85, 0) * mm});
            skLineSegment(sketch, "E247", {"start": v(141.85, 0) * mm, "end": v(144.85, 0) * mm});
            skLineSegment(sketch, "E248", {"start": v(144.85, 0) * mm, "end": v(144.85, 30) * mm});
            skLineSegment(sketch, "E249", {"start": v(144.85, 30) * mm, "end": v(141.85, 30) * mm});
            skLineSegment(sketch, "E250", {"start": v(141.85, 30) * mm, "end": v(141.85, 57) * mm});
            skLineSegment(sketch, "E251", {"start": v(141.85, 57) * mm, "end": v(144.85, 57) * mm});
            skLineSegment(sketch, "E252", {"start": v(144.85, 60) * mm, "end": v(123.64, 81.21) * mm});
            skLineSegment(sketch, "E253", {"start": v(123.64, 81.21) * mm, "end": v(121.52, 79.1) * mm});
            skLineSegment(sketch, "E254", {"start": v(121.52, 79.1) * mm, "end": v(100.3, 100.3) * mm});
            skLineSegment(sketch, "E255", {"start": v(100.3, 100.3) * mm, "end": v(102.42, 102.43) * mm});
            skLineSegment(sketch, "E256", {"start": v(102.42, 102.43) * mm, "end": v(81.21, 123.64) * mm});
            skLineSegment(sketch, "E257", {"start": v(81.21, 123.64) * mm, "end": v(79.09, 121.52) * mm});
            skLineSegment(sketch, "E258", {"start": v(79.09, 121.52) * mm, "end": v(60, 140.6) * mm});
            skLineSegment(sketch, "E259", {"start": v(60, 140.6) * mm, "end": v(62.12, 142.73) * mm});
            skLineSegment(sketch, "E260", {"start": v(60, 144.85) * mm, "end": v(30, 144.85) * mm});
            skLineSegment(sketch, "E261", {"start": v(30, 144.85) * mm, "end": v(30, 141.85) * mm});
            skLineSegment(sketch, "E262", {"start": v(30, 141.85) * mm, "end": v(0, 141.85) * mm});
            skLineSegment(sketch, "E263", {"start": v(0, 141.85) * mm, "end": v(0, 144.85) * mm});
            skLineSegment(sketch, "E264", {"start": v(0, 144.85) * mm, "end": v(-30, 144.85) * mm});
            skLineSegment(sketch, "E265", {"start": v(-30, 144.85) * mm, "end": v(-30, 141.85) * mm});
            skLineSegment(sketch, "E266", {"start": v(-30, 141.85) * mm, "end": v(-57, 141.85) * mm});
            skLineSegment(sketch, "E267", {"start": v(-57, 141.85) * mm, "end": v(-57, 144.85) * mm});
            skLineSegment(sketch, "E268", {"start": v(-60, 144.85) * mm, "end": v(-81.21, 123.64) * mm});
            skLineSegment(sketch, "E269", {"start": v(-81.21, 123.64) * mm, "end": v(-79.1, 121.52) * mm});
            skLineSegment(sketch, "E270", {"start": v(-79.1, 121.52) * mm, "end": v(-100.3, 100.3) * mm});
            skLineSegment(sketch, "E271", {"start": v(-100.3, 100.3) * mm, "end": v(-102.43, 102.42) * mm});
            skLineSegment(sketch, "E272", {"start": v(-102.43, 102.42) * mm, "end": v(-123.64, 81.21) * mm});
            skLineSegment(sketch, "E273", {"start": v(-123.64, 81.21) * mm, "end": v(-121.52, 79.09) * mm});
            skLineSegment(sketch, "E274", {"start": v(-121.52, 79.09) * mm, "end": v(-140.6, 60) * mm});
            skLineSegment(sketch, "E275", {"start": v(-140.6, 60) * mm, "end": v(-142.73, 62.12) * mm});
            skLineSegment(sketch, "E276", {"start": v(-144.85, 60) * mm, "end": v(-144.85, 30) * mm});
            skLineSegment(sketch, "E277", {"start": v(-144.85, 30) * mm, "end": v(-141.85, 30) * mm});
            skLineSegment(sketch, "E278", {"start": v(-141.85, 30) * mm, "end": v(-141.85, 0) * mm});
            skLineSegment(sketch, "E279", {"start": v(-141.85, 0) * mm, "end": v(-144.85, 0) * mm});
            skLineSegment(sketch, "E280", {"start": v(-144.85, 0) * mm, "end": v(-144.85, -30) * mm});
            skLineSegment(sketch, "E281", {"start": v(-144.85, -30) * mm, "end": v(-141.85, -30) * mm});
            skLineSegment(sketch, "E282", {"start": v(-141.85, -30) * mm, "end": v(-141.85, -57) * mm});
            skLineSegment(sketch, "E283", {"start": v(-141.85, -57) * mm, "end": v(-144.85, -57) * mm});
            skLineSegment(sketch, "E284", {"start": v(-144.85, -60) * mm, "end": v(-123.64, -81.21) * mm});
            skLineSegment(sketch, "E285", {"start": v(-123.64, -81.21) * mm, "end": v(-121.52, -79.1) * mm});
            skLineSegment(sketch, "E286", {"start": v(-121.52, -79.1) * mm, "end": v(-100.3, -100.3) * mm});
            skLineSegment(sketch, "E287", {"start": v(-100.3, -100.3) * mm, "end": v(-102.42, -102.43) * mm});
            skLineSegment(sketch, "E288", {"start": v(-102.42, -102.43) * mm, "end": v(-81.21, -123.64) * mm});
            skLineSegment(sketch, "E289", {"start": v(-81.21, -123.64) * mm, "end": v(-79.09, -121.52) * mm});
            skLineSegment(sketch, "E290", {"start": v(-79.09, -121.52) * mm, "end": v(-60, -140.6) * mm});
            skLineSegment(sketch, "E291", {"start": v(-60, -140.6) * mm, "end": v(-62.12, -142.73) * mm});
            skLineSegment(sketch, "E292.trimOffspring", {"start": v(-81.21, -123.64) * mm, "end": v(-102.42, -102.42) * mm});
            skLineSegment(sketch, "E293.trimOffspring", {"start": v(-123.64, -81.21) * mm, "end": v(-144.85, -60) * mm});
            skLineSegment(sketch, "E294.trimOffspring", {"start": v(-144.85, -30) * mm, "end": v(-144.85, 0) * mm});
            skLineSegment(sketch, "E295.trimOffspring", {"start": v(-144.85, 30) * mm, "end": v(-144.85, 60) * mm});
            skLineSegment(sketch, "E296.trimOffspring", {"start": v(-123.64, 81.21) * mm, "end": v(-102.42, 102.42) * mm});
            skLineSegment(sketch, "E297.trimOffspring", {"start": v(-81.21, 123.64) * mm, "end": v(-60, 144.85) * mm});
            skLineSegment(sketch, "E298.trimOffspring", {"start": v(-30, 144.85) * mm, "end": v(0, 144.85) * mm});
            skLineSegment(sketch, "E299.trimOffspring", {"start": v(30, 144.85) * mm, "end": v(60, 144.85) * mm});
            skLineSegment(sketch, "E300", {"start": v(0, 144.85) * mm, "end": v(30, 144.85) * mm, "construction": true});
            skLineSegment(sketch, "E301.trimOffspring", {"start": v(81.21, 123.64) * mm, "end": v(102.42, 102.42) * mm});
            skLineSegment(sketch, "E302.trimOffspring", {"start": v(123.64, 81.21) * mm, "end": v(144.85, 60) * mm});
            skLineSegment(sketch, "E303", {"start": v(102.42, 102.42) * mm, "end": v(123.64, 81.21) * mm, "construction": true});
            skLineSegment(sketch, "E304.trimOffspring", {"start": v(81.21, -123.64) * mm, "end": v(60, -144.85) * mm});
            skLineSegment(sketch, "E305.trimOffspring", {"start": v(123.64, -81.21) * mm, "end": v(102.42, -102.42) * mm});
            skLineSegment(sketch, "E306.trimOffspring", {"start": v(144.85, -30) * mm, "end": v(144.85, -60) * mm});
            skLineSegment(sketch, "E307.trimOffspring", {"start": v(144.85, 30) * mm, "end": v(144.85, 0) * mm});
            skLineSegment(sketch, "E308", {"start": v(144.85, -30) * mm, "end": v(144.85, 0) * mm, "construction": true});
            skLineSegment(sketch, "E309", {"start": v(144.85, 30) * mm, "end": v(144.85, 57) * mm, "construction": true});
            skLineSegment(sketch, "E310.bottom", {"start": v(-40, 114.46) * mm, "end": v(40, 114.46) * mm});
            skLineSegment(sketch, "E310.top", {"start": v(-40, 99.46) * mm, "end": v(40, 99.46) * mm});
            skLineSegment(sketch, "E310.left", {"start": v(-40, 114.46) * mm, "end": v(-40, 99.46) * mm});
            skLineSegment(sketch, "E310.right", {"start": v(40, 114.46) * mm, "end": v(40, 99.46) * mm});
            skPoint(sketch, "E310.middle", {"position": v(0, 106.96) * mm});
            skPoint(sketch, "E311.MirrorP", {"position": v(0, -106.96) * mm});
            skLineSegment(sketch, "E312.MirrorCS", {"start": v(-40, -114.46) * mm, "end": v(40, -114.46) * mm});
            skLineSegment(sketch, "E313.MirrorCS", {"start": v(-40, -99.46) * mm, "end": v(40, -99.46) * mm});
            skLineSegment(sketch, "E314.MirrorCS", {"start": v(-40, -114.46) * mm, "end": v(-40, -99.46) * mm});
            skLineSegment(sketch, "E315.MirrorCS", {"start": v(40, -114.46) * mm, "end": v(40, -99.46) * mm});
            skLineSegment(sketch, "E316", {"start": v(-104.85, 42.5) * mm, "end": v(-104.85, 48.5) * mm, "construction": true});
            skLineSegment(sketch, "E317", {"start": v(-104.85, 48.5) * mm, "end": v(-101.85, 48.5) * mm});
            skLineSegment(sketch, "E318", {"start": v(-101.85, 48.5) * mm, "end": v(-101.85, 45.5) * mm});
            skLineSegment(sketch, "E319", {"start": v(-101.85, 45.5) * mm, "end": v(-104.85, 45.5) * mm});
            skLineSegment(sketch, "E320", {"start": v(-104.85, 45.5) * mm, "end": v(-104.85, 48.5) * mm});
            skLineSegment(sketch, "E321", {"start": v(-101.85, 48.5) * mm, "end": v(-98.85, 48.5) * mm, "construction": true});
            skLineSegment(sketch, "E322", {"start": v(-98.85, 48.5) * mm, "end": v(-95.85, 48.5) * mm, "construction": true});
            skLineSegment(sketch, "E323", {"start": v(-95.85, 48.5) * mm, "end": v(-92.85, 48.5) * mm, "construction": true});
            skLineSegment(sketch, "E324", {"start": v(-92.85, 48.5) * mm, "end": v(-89.85, 48.5) * mm, "construction": true});
            skLineSegment(sketch, "E325", {"start": v(-89.85, 48.5) * mm, "end": v(-86.85, 48.5) * mm, "construction": true});
            skLineSegment(sketch, "E326", {"start": v(-86.85, 48.5) * mm, "end": v(-83.85, 48.5) * mm, "construction": true});
            skLineSegment(sketch, "E327", {"start": v(-83.85, 48.5) * mm, "end": v(-80.85, 48.5) * mm, "construction": true});
            skLineSegment(sketch, "E328", {"start": v(-80.85, 48.5) * mm, "end": v(-77.85, 48.5) * mm, "construction": true});
            skLineSegment(sketch, "E329", {"start": v(-77.85, 48.5) * mm, "end": v(-74.85, 48.5) * mm, "construction": true});
            skLineSegment(sketch, "E330", {"start": v(-74.85, 48.5) * mm, "end": v(-71.85, 48.5) * mm, "construction": true});
            skLineSegment(sketch, "E331", {"start": v(-71.85, 48.5) * mm, "end": v(-68.85, 48.5) * mm, "construction": true});
            skLineSegment(sketch, "E332", {"start": v(-68.85, 48.5) * mm, "end": v(-65.85, 48.5) * mm, "construction": true});
            skLineSegment(sketch, "E333", {"start": v(-65.85, 48.5) * mm, "end": v(-62.85, 48.5) * mm, "construction": true});
            skLineSegment(sketch, "E334", {"start": v(-98.85, 48.5) * mm, "end": v(-98.85, 45.5) * mm});
            skLineSegment(sketch, "E335", {"start": v(-98.85, 45.5) * mm, "end": v(-95.85, 45.5) * mm});
            skLineSegment(sketch, "E336", {"start": v(-95.85, 45.5) * mm, "end": v(-95.85, 48.5) * mm});
            skLineSegment(sketch, "E337", {"start": v(-95.85, 48.5) * mm, "end": v(-98.85, 48.5) * mm});
            skLineSegment(sketch, "E338", {"start": v(-92.85, 48.5) * mm, "end": v(-92.85, 45.5) * mm});
            skLineSegment(sketch, "E339", {"start": v(-92.85, 45.5) * mm, "end": v(-89.85, 45.5) * mm});
            skLineSegment(sketch, "E340", {"start": v(-89.85, 45.5) * mm, "end": v(-89.85, 48.5) * mm});
            skLineSegment(sketch, "E341", {"start": v(-92.85, 48.5) * mm, "end": v(-89.85, 48.5) * mm});
            skLineSegment(sketch, "E342", {"start": v(-86.85, 48.5) * mm, "end": v(-86.85, 45.5) * mm});
            skLineSegment(sketch, "E343", {"start": v(-86.85, 45.5) * mm, "end": v(-83.85, 45.5) * mm});
            skLineSegment(sketch, "E344", {"start": v(-86.85, 48.5) * mm, "end": v(-83.85, 48.5) * mm});
            skLineSegment(sketch, "E345", {"start": v(-83.85, 45.5) * mm, "end": v(-83.85, 48.5) * mm});
            skLineSegment(sketch, "E346", {"start": v(-80.85, 48.5) * mm, "end": v(-80.85, 45.5) * mm});
            skLineSegment(sketch, "E347", {"start": v(-80.85, 45.5) * mm, "end": v(-77.85, 45.5) * mm});
            skLineSegment(sketch, "E348", {"start": v(-77.85, 45.5) * mm, "end": v(-77.85, 48.5) * mm});
            skLineSegment(sketch, "E349", {"start": v(-80.85, 48.5) * mm, "end": v(-77.85, 48.5) * mm});
            skLineSegment(sketch, "E350", {"start": v(-74.85, 48.5) * mm, "end": v(-74.85, 45.5) * mm});
            skLineSegment(sketch, "E351", {"start": v(-74.85, 45.5) * mm, "end": v(-71.85, 45.5) * mm});
            skLineSegment(sketch, "E352", {"start": v(-71.85, 45.5) * mm, "end": v(-71.85, 48.5) * mm});
            skLineSegment(sketch, "E353", {"start": v(-74.85, 48.5) * mm, "end": v(-71.85, 48.5) * mm});
            skLineSegment(sketch, "E354", {"start": v(-68.85, 48.5) * mm, "end": v(-68.85, 45.5) * mm});
            skLineSegment(sketch, "E355", {"start": v(-68.85, 45.5) * mm, "end": v(-65.85, 45.5) * mm});
            skLineSegment(sketch, "E356", {"start": v(-65.85, 45.5) * mm, "end": v(-65.85, 48.5) * mm});
            skLineSegment(sketch, "E357", {"start": v(-68.85, 48.5) * mm, "end": v(-65.85, 48.5) * mm});
            skLineSegment(sketch, "E358.MirrorCS", {"start": v(-92.85, -48.5) * mm, "end": v(-89.85, -48.5) * mm});
            skLineSegment(sketch, "E359.MirrorCS", {"start": v(-92.85, -48.5) * mm, "end": v(-89.85, -48.5) * mm, "construction": true});
            skLineSegment(sketch, "E360.MirrorCS", {"start": v(-71.85, -48.5) * mm, "end": v(-68.85, -48.5) * mm, "construction": true});
            skLineSegment(sketch, "E361.MirrorCS", {"start": v(-65.85, -45.5) * mm, "end": v(-65.85, -48.5) * mm});
            skLineSegment(sketch, "E362.MirrorCS", {"start": v(-89.85, -45.5) * mm, "end": v(-89.85, -48.5) * mm});
            skLineSegment(sketch, "E363.MirrorCS", {"start": v(-86.85, -48.5) * mm, "end": v(-86.85, -45.5) * mm});
            skLineSegment(sketch, "E364.MirrorCS", {"start": v(-83.85, -45.5) * mm, "end": v(-83.85, -48.5) * mm});
            skLineSegment(sketch, "E365.MirrorCS", {"start": v(-80.85, -48.5) * mm, "end": v(-80.85, -45.5) * mm});
            skLineSegment(sketch, "E366.MirrorCS", {"start": v(-77.85, -45.5) * mm, "end": v(-77.85, -48.5) * mm});
            skLineSegment(sketch, "E367.MirrorCS", {"start": v(-74.85, -48.5) * mm, "end": v(-74.85, -45.5) * mm});
            skLineSegment(sketch, "E368.MirrorCS", {"start": v(-98.85, -48.5) * mm, "end": v(-98.85, -45.5) * mm});
            skLineSegment(sketch, "E369.MirrorCS", {"start": v(-101.85, -48.5) * mm, "end": v(-101.85, -45.5) * mm});
            skLineSegment(sketch, "E370.MirrorCS", {"start": v(-71.85, -45.5) * mm, "end": v(-71.85, -48.5) * mm});
            skLineSegment(sketch, "E371.MirrorCS", {"start": v(-95.85, -45.5) * mm, "end": v(-95.85, -48.5) * mm});
            skLineSegment(sketch, "E372.MirrorCS", {"start": v(-104.85, -45.5) * mm, "end": v(-104.85, -48.5) * mm});
            skLineSegment(sketch, "E373.MirrorCS", {"start": v(-68.85, -48.5) * mm, "end": v(-68.85, -45.5) * mm});
            skLineSegment(sketch, "E374.MirrorCS", {"start": v(-92.85, -48.5) * mm, "end": v(-92.85, -45.5) * mm});
            skLineSegment(sketch, "E375.MirrorCS", {"start": v(-92.85, -45.5) * mm, "end": v(-89.85, -45.5) * mm});
            skLineSegment(sketch, "E376.MirrorCS", {"start": v(-68.85, -48.5) * mm, "end": v(-65.85, -48.5) * mm});
            skLineSegment(sketch, "E377.MirrorCS", {"start": v(-86.85, -48.5) * mm, "end": v(-83.85, -48.5) * mm});
            skLineSegment(sketch, "E378.MirrorCS", {"start": v(-80.85, -48.5) * mm, "end": v(-77.85, -48.5) * mm});
            skLineSegment(sketch, "E379.MirrorCS", {"start": v(-74.85, -48.5) * mm, "end": v(-71.85, -48.5) * mm});
            skLineSegment(sketch, "E380.MirrorCS", {"start": v(-95.85, -48.5) * mm, "end": v(-98.85, -48.5) * mm});
            skLineSegment(sketch, "E381.MirrorCS", {"start": v(-95.85, -48.5) * mm, "end": v(-92.85, -48.5) * mm, "construction": true});
            skLineSegment(sketch, "E382.MirrorCS", {"start": v(-89.85, -48.5) * mm, "end": v(-86.85, -48.5) * mm, "construction": true});
            skLineSegment(sketch, "E383.MirrorCS", {"start": v(-86.85, -48.5) * mm, "end": v(-83.85, -48.5) * mm, "construction": true});
            skLineSegment(sketch, "E384.MirrorCS", {"start": v(-83.85, -48.5) * mm, "end": v(-80.85, -48.5) * mm, "construction": true});
            skLineSegment(sketch, "E385.MirrorCS", {"start": v(-86.85, -45.5) * mm, "end": v(-83.85, -45.5) * mm});
            skLineSegment(sketch, "E386.MirrorCS", {"start": v(-80.85, -48.5) * mm, "end": v(-77.85, -48.5) * mm, "construction": true});
            skLineSegment(sketch, "E387.MirrorCS", {"start": v(-77.85, -48.5) * mm, "end": v(-74.85, -48.5) * mm, "construction": true});
            skLineSegment(sketch, "E388.MirrorCS", {"start": v(-74.85, -48.5) * mm, "end": v(-71.85, -48.5) * mm, "construction": true});
            skLineSegment(sketch, "E389.MirrorCS", {"start": v(-80.85, -45.5) * mm, "end": v(-77.85, -45.5) * mm});
            skLineSegment(sketch, "E390.MirrorCS", {"start": v(-68.85, -48.5) * mm, "end": v(-65.85, -48.5) * mm, "construction": true});
            skLineSegment(sketch, "E391.MirrorCS", {"start": v(-65.85, -48.5) * mm, "end": v(-62.85, -48.5) * mm, "construction": true});
            skLineSegment(sketch, "E392.MirrorCS", {"start": v(-104.85, -48.5) * mm, "end": v(-101.85, -48.5) * mm});
            skLineSegment(sketch, "E393.MirrorCS", {"start": v(-74.85, -45.5) * mm, "end": v(-71.85, -45.5) * mm});
            skLineSegment(sketch, "E394.MirrorCS", {"start": v(-101.85, -45.5) * mm, "end": v(-104.85, -45.5) * mm});
            skLineSegment(sketch, "E395.MirrorCS", {"start": v(-98.85, -45.5) * mm, "end": v(-95.85, -45.5) * mm});
            skLineSegment(sketch, "E396.MirrorCS", {"start": v(-101.85, -48.5) * mm, "end": v(-98.85, -48.5) * mm, "construction": true});
            skLineSegment(sketch, "E397.MirrorCS", {"start": v(-98.85, -48.5) * mm, "end": v(-95.85, -48.5) * mm, "construction": true});
            skLineSegment(sketch, "E398.MirrorCS", {"start": v(-68.85, -45.5) * mm, "end": v(-65.85, -45.5) * mm});
            skLineSegment(sketch, "E399", {"start": v(0, 144.85) * mm, "end": v(0, 90.23) * mm, "construction": true});
            skLineSegment(sketch, "E400.MirrorCS", {"start": v(92.85, -48.5) * mm, "end": v(89.85, -48.5) * mm});
            skLineSegment(sketch, "E401.MirrorCS", {"start": v(68.85, -48.5) * mm, "end": v(65.85, -48.5) * mm});
            skLineSegment(sketch, "E402.MirrorCS", {"start": v(86.85, -48.5) * mm, "end": v(83.85, -48.5) * mm});
            skLineSegment(sketch, "E403.MirrorCS", {"start": v(80.85, -48.5) * mm, "end": v(77.85, -48.5) * mm});
            skLineSegment(sketch, "E404.MirrorCS", {"start": v(74.85, -48.5) * mm, "end": v(71.85, -48.5) * mm});
            skLineSegment(sketch, "E405.MirrorCS", {"start": v(95.85, -48.5) * mm, "end": v(98.85, -48.5) * mm});
            skLineSegment(sketch, "E406.MirrorCS", {"start": v(68.85, -48.5) * mm, "end": v(68.85, -45.5) * mm});
            skLineSegment(sketch, "E407.MirrorCS", {"start": v(80.85, -45.5) * mm, "end": v(77.85, -45.5) * mm});
            skLineSegment(sketch, "E408.MirrorCS", {"start": v(68.85, -48.5) * mm, "end": v(65.85, -48.5) * mm, "construction": true});
            skLineSegment(sketch, "E409.MirrorCS", {"start": v(92.85, -48.5) * mm, "end": v(92.85, -45.5) * mm});
            skLineSegment(sketch, "E410.MirrorCS", {"start": v(65.85, -48.5) * mm, "end": v(62.85, -48.5) * mm, "construction": true});
            skLineSegment(sketch, "E411.MirrorCS", {"start": v(92.85, -45.5) * mm, "end": v(89.85, -45.5) * mm});
            skLineSegment(sketch, "E412.MirrorCS", {"start": v(92.85, -48.5) * mm, "end": v(89.85, -48.5) * mm, "construction": true});
            skLineSegment(sketch, "E413.MirrorCS", {"start": v(104.85, -48.5) * mm, "end": v(101.85, -48.5) * mm});
            skLineSegment(sketch, "E414.MirrorCS", {"start": v(71.85, -48.5) * mm, "end": v(68.85, -48.5) * mm, "construction": true});
            skLineSegment(sketch, "E415.MirrorCS", {"start": v(74.85, -45.5) * mm, "end": v(71.85, -45.5) * mm});
            skLineSegment(sketch, "E416.MirrorCS", {"start": v(65.85, -45.5) * mm, "end": v(65.85, -48.5) * mm});
            skLineSegment(sketch, "E417.MirrorCS", {"start": v(101.85, -45.5) * mm, "end": v(104.85, -45.5) * mm});
            skLineSegment(sketch, "E418.MirrorCS", {"start": v(89.85, -45.5) * mm, "end": v(89.85, -48.5) * mm});
            skLineSegment(sketch, "E419.MirrorCS", {"start": v(98.85, -45.5) * mm, "end": v(95.85, -45.5) * mm});
            skLineSegment(sketch, "E420.MirrorCS", {"start": v(86.85, -48.5) * mm, "end": v(86.85, -45.5) * mm});
            skLineSegment(sketch, "E421.MirrorCS", {"start": v(101.85, -48.5) * mm, "end": v(98.85, -48.5) * mm, "construction": true});
            skLineSegment(sketch, "E422.MirrorCS", {"start": v(83.85, -45.5) * mm, "end": v(83.85, -48.5) * mm});
            skLineSegment(sketch, "E423.MirrorCS", {"start": v(80.85, -48.5) * mm, "end": v(80.85, -45.5) * mm});
            skLineSegment(sketch, "E424.MirrorCS", {"start": v(98.85, -48.5) * mm, "end": v(95.85, -48.5) * mm, "construction": true});
            skLineSegment(sketch, "E425.MirrorCS", {"start": v(95.85, -48.5) * mm, "end": v(92.85, -48.5) * mm, "construction": true});
            skLineSegment(sketch, "E426.MirrorCS", {"start": v(77.85, -45.5) * mm, "end": v(77.85, -48.5) * mm});
            skLineSegment(sketch, "E427.MirrorCS", {"start": v(68.85, -45.5) * mm, "end": v(65.85, -45.5) * mm});
            skLineSegment(sketch, "E428.MirrorCS", {"start": v(89.85, -48.5) * mm, "end": v(86.85, -48.5) * mm, "construction": true});
            skLineSegment(sketch, "E429.MirrorCS", {"start": v(74.85, -48.5) * mm, "end": v(74.85, -45.5) * mm});
            skLineSegment(sketch, "E430.MirrorCS", {"start": v(86.85, -48.5) * mm, "end": v(83.85, -48.5) * mm, "construction": true});
            skLineSegment(sketch, "E431.MirrorCS", {"start": v(98.85, -48.5) * mm, "end": v(98.85, -45.5) * mm});
            skLineSegment(sketch, "E432.MirrorCS", {"start": v(83.85, -48.5) * mm, "end": v(80.85, -48.5) * mm, "construction": true});
            skLineSegment(sketch, "E433.MirrorCS", {"start": v(101.85, -48.5) * mm, "end": v(101.85, -45.5) * mm});
            skLineSegment(sketch, "E434.MirrorCS", {"start": v(86.85, -45.5) * mm, "end": v(83.85, -45.5) * mm});
            skLineSegment(sketch, "E435.MirrorCS", {"start": v(71.85, -45.5) * mm, "end": v(71.85, -48.5) * mm});
            skLineSegment(sketch, "E436.MirrorCS", {"start": v(80.85, -48.5) * mm, "end": v(77.85, -48.5) * mm, "construction": true});
            skLineSegment(sketch, "E437.MirrorCS", {"start": v(104.85, -45.5) * mm, "end": v(104.85, -48.5) * mm});
            skLineSegment(sketch, "E438.MirrorCS", {"start": v(74.85, -48.5) * mm, "end": v(71.85, -48.5) * mm, "construction": true});
            skLineSegment(sketch, "E439.MirrorCS", {"start": v(77.85, -48.5) * mm, "end": v(74.85, -48.5) * mm, "construction": true});
            skLineSegment(sketch, "E440.MirrorCS", {"start": v(95.85, -45.5) * mm, "end": v(95.85, -48.5) * mm});
            skLineSegment(sketch, "E441.MirrorCS", {"start": v(80.85, 48.5) * mm, "end": v(77.85, 48.5) * mm});
            skLineSegment(sketch, "E442.MirrorCS", {"start": v(86.85, 48.5) * mm, "end": v(83.85, 48.5) * mm});
            skLineSegment(sketch, "E443.MirrorCS", {"start": v(92.85, 48.5) * mm, "end": v(89.85, 48.5) * mm});
            skLineSegment(sketch, "E444.MirrorCS", {"start": v(68.85, 48.5) * mm, "end": v(65.85, 48.5) * mm});
            skLineSegment(sketch, "E445.MirrorCS", {"start": v(74.85, 48.5) * mm, "end": v(71.85, 48.5) * mm});
            skLineSegment(sketch, "E446.MirrorCS", {"start": v(95.85, 48.5) * mm, "end": v(98.85, 48.5) * mm});
            skLineSegment(sketch, "E447.MirrorCS", {"start": v(68.85, 48.5) * mm, "end": v(65.85, 48.5) * mm, "construction": true});
            skLineSegment(sketch, "E448.MirrorCS", {"start": v(71.85, 48.5) * mm, "end": v(68.85, 48.5) * mm, "construction": true});
            skLineSegment(sketch, "E449.MirrorCS", {"start": v(74.85, 48.5) * mm, "end": v(71.85, 48.5) * mm, "construction": true});
            skLineSegment(sketch, "E450.MirrorCS", {"start": v(77.85, 48.5) * mm, "end": v(74.85, 48.5) * mm, "construction": true});
            skLineSegment(sketch, "E451.MirrorCS", {"start": v(80.85, 48.5) * mm, "end": v(77.85, 48.5) * mm, "construction": true});
            skLineSegment(sketch, "E452.MirrorCS", {"start": v(83.85, 48.5) * mm, "end": v(80.85, 48.5) * mm, "construction": true});
            skLineSegment(sketch, "E453.MirrorCS", {"start": v(86.85, 48.5) * mm, "end": v(83.85, 48.5) * mm, "construction": true});
            skLineSegment(sketch, "E454.MirrorCS", {"start": v(89.85, 48.5) * mm, "end": v(86.85, 48.5) * mm, "construction": true});
            skLineSegment(sketch, "E455.MirrorCS", {"start": v(92.85, 48.5) * mm, "end": v(89.85, 48.5) * mm, "construction": true});
            skLineSegment(sketch, "E456.MirrorCS", {"start": v(95.85, 48.5) * mm, "end": v(92.85, 48.5) * mm, "construction": true});
            skLineSegment(sketch, "E457.MirrorCS", {"start": v(98.85, 48.5) * mm, "end": v(95.85, 48.5) * mm, "construction": true});
            skLineSegment(sketch, "E458.MirrorCS", {"start": v(104.85, 48.5) * mm, "end": v(101.85, 48.5) * mm});
            skLineSegment(sketch, "E459.MirrorCS", {"start": v(101.85, 48.5) * mm, "end": v(98.85, 48.5) * mm, "construction": true});
            skLineSegment(sketch, "E460.MirrorCS", {"start": v(101.85, 45.5) * mm, "end": v(104.85, 45.5) * mm});
            skLineSegment(sketch, "E461.MirrorCS", {"start": v(98.85, 45.5) * mm, "end": v(95.85, 45.5) * mm});
            skLineSegment(sketch, "E462.MirrorCS", {"start": v(74.85, 45.5) * mm, "end": v(71.85, 45.5) * mm});
            skLineSegment(sketch, "E463.MirrorCS", {"start": v(98.85, 48.5) * mm, "end": v(98.85, 45.5) * mm});
            skLineSegment(sketch, "E464.MirrorCS", {"start": v(101.85, 48.5) * mm, "end": v(101.85, 45.5) * mm});
            skLineSegment(sketch, "E465.MirrorCS", {"start": v(74.85, 48.5) * mm, "end": v(74.85, 45.5) * mm});
            skLineSegment(sketch, "E466.MirrorCS", {"start": v(77.85, 45.5) * mm, "end": v(77.85, 48.5) * mm});
            skLineSegment(sketch, "E467.MirrorCS", {"start": v(80.85, 45.5) * mm, "end": v(77.85, 45.5) * mm});
            skLineSegment(sketch, "E468.MirrorCS", {"start": v(80.85, 48.5) * mm, "end": v(80.85, 45.5) * mm});
            skLineSegment(sketch, "E469.MirrorCS", {"start": v(83.85, 45.5) * mm, "end": v(83.85, 48.5) * mm});
            skLineSegment(sketch, "E470.MirrorCS", {"start": v(86.85, 45.5) * mm, "end": v(83.85, 45.5) * mm});
            skLineSegment(sketch, "E471.MirrorCS", {"start": v(86.85, 48.5) * mm, "end": v(86.85, 45.5) * mm});
            skLineSegment(sketch, "E472.MirrorCS", {"start": v(65.85, 45.5) * mm, "end": v(65.85, 48.5) * mm});
            skLineSegment(sketch, "E473.MirrorCS", {"start": v(89.85, 45.5) * mm, "end": v(89.85, 48.5) * mm});
            skLineSegment(sketch, "E474.MirrorCS", {"start": v(92.85, 45.5) * mm, "end": v(89.85, 45.5) * mm});
            skLineSegment(sketch, "E475.MirrorCS", {"start": v(68.85, 45.5) * mm, "end": v(65.85, 45.5) * mm});
            skLineSegment(sketch, "E476.MirrorCS", {"start": v(71.85, 45.5) * mm, "end": v(71.85, 48.5) * mm});
            skLineSegment(sketch, "E477.MirrorCS", {"start": v(95.85, 45.5) * mm, "end": v(95.85, 48.5) * mm});
            skLineSegment(sketch, "E478.MirrorCS", {"start": v(104.85, 45.5) * mm, "end": v(104.85, 48.5) * mm});
            skLineSegment(sketch, "E479.MirrorCS", {"start": v(68.85, 48.5) * mm, "end": v(68.85, 45.5) * mm});
            skLineSegment(sketch, "E480.MirrorCS", {"start": v(92.85, 48.5) * mm, "end": v(92.85, 45.5) * mm});
            skLineSegment(sketch, "E481.MirrorCS", {"start": v(65.85, 48.5) * mm, "end": v(62.85, 48.5) * mm, "construction": true});
            skLineSegment(sketch, "E482", {"start": v(0, 90.23) * mm, "end": v(-40, 90.23) * mm, "construction": true});
            skLineSegment(sketch, "E483.trimOffspring", {"start": v(0, -90.23) * mm, "end": v(0, -141.85) * mm, "construction": true});
            skLineSegment(sketch, "E484", {"start": v(-8.85, 12.5) * mm, "end": v(-8.85, -12.5) * mm, "construction": true});
            skLineSegment(sketch, "E485", {"start": v(8.85, 12.5) * mm, "end": v(8.85, -12.5) * mm, "construction": true});
            skCircle(sketch, "E486", {"center": v(0, 0) * mm, "radius": 7.5 * mm});
            skLineSegment(sketch, "E487", {"start": v(0, -84.23) * mm, "end": v(45, -84.23) * mm, "construction": true});
            skLineSegment(sketch, "E488", {"start": v(45, -84.23) * mm, "end": v(45, -90.23) * mm});
            skLineSegment(sketch, "E489", {"start": v(45, -90.23) * mm, "end": v(35, -90.23) * mm});
            skLineSegment(sketch, "E490", {"start": v(35, -90.23) * mm, "end": v(35, -84.23) * mm});
            skLineSegment(sketch, "E491", {"start": v(35, -84.23) * mm, "end": v(45, -84.23) * mm});
            skLineSegment(sketch, "E492", {"start": v(35, -84.23) * mm, "end": v(25, -84.23) * mm, "construction": true});
            skLineSegment(sketch, "E493", {"start": v(25, -84.23) * mm, "end": v(25, -90.23) * mm});
            skLineSegment(sketch, "E494", {"start": v(25, -90.23) * mm, "end": v(15, -90.23) * mm});
            skLineSegment(sketch, "E495", {"start": v(15, -90.23) * mm, "end": v(15, -84.23) * mm});
            skLineSegment(sketch, "E496", {"start": v(15, -84.23) * mm, "end": v(25, -84.23) * mm});
            skLineSegment(sketch, "E497", {"start": v(15, -84.23) * mm, "end": v(5, -84.23) * mm, "construction": true});
            skLineSegment(sketch, "E498", {"start": v(5, -84.23) * mm, "end": v(5, -90.23) * mm});
            skLineSegment(sketch, "E499", {"start": v(5, -90.23) * mm, "end": v(-5, -90.23) * mm});
            skLineSegment(sketch, "E500", {"start": v(-5, -90.23) * mm, "end": v(-5, -84.23) * mm});
            skLineSegment(sketch, "E501", {"start": v(-5, -84.23) * mm, "end": v(5, -84.23) * mm});
            skLineSegment(sketch, "E502", {"start": v(-5, -84.23) * mm, "end": v(-15, -84.23) * mm, "construction": true});
            skLineSegment(sketch, "E503", {"start": v(-15, -84.23) * mm, "end": v(-15, -90.23) * mm});
            skLineSegment(sketch, "E504", {"start": v(-15, -90.23) * mm, "end": v(-25, -90.23) * mm});
            skLineSegment(sketch, "E505", {"start": v(-25, -90.23) * mm, "end": v(-25, -84.23) * mm});
            skLineSegment(sketch, "E506", {"start": v(-25, -84.23) * mm, "end": v(-15, -84.23) * mm});
            skLineSegment(sketch, "E507", {"start": v(-25, -84.23) * mm, "end": v(-35, -84.23) * mm, "construction": true});
            skLineSegment(sketch, "E508", {"start": v(-35, -84.23) * mm, "end": v(-45, -84.23) * mm});
            skLineSegment(sketch, "E509", {"start": v(-45, -84.23) * mm, "end": v(-45, -90.23) * mm});
            skLineSegment(sketch, "E510", {"start": v(-45, -90.23) * mm, "end": v(-35, -90.23) * mm});
            skLineSegment(sketch, "E511", {"start": v(-35, -90.23) * mm, "end": v(-35, -84.23) * mm});
            skLineSegment(sketch, "E512.trimOffspring", {"start": v(0, 84.23) * mm, "end": v(0, -84.85) * mm, "construction": true});
            skLineSegment(sketch, "E513.MirrorCS", {"start": v(-35, 90.23) * mm, "end": v(-35, 84.23) * mm});
            skLineSegment(sketch, "E514.MirrorCS", {"start": v(-45, 90.23) * mm, "end": v(-35, 90.23) * mm});
            skLineSegment(sketch, "E515.MirrorCS", {"start": v(-45, 84.23) * mm, "end": v(-45, 90.23) * mm});
            skLineSegment(sketch, "E516.MirrorCS", {"start": v(-35, 84.23) * mm, "end": v(-45, 84.23) * mm});
            skLineSegment(sketch, "E517.MirrorCS", {"start": v(-25, 84.23) * mm, "end": v(-35, 84.23) * mm, "construction": true});
            skLineSegment(sketch, "E518.MirrorCS", {"start": v(-25, 84.23) * mm, "end": v(-15, 84.23) * mm});
            skLineSegment(sketch, "E519.MirrorCS", {"start": v(-25, 90.23) * mm, "end": v(-25, 84.23) * mm});
            skLineSegment(sketch, "E520.MirrorCS", {"start": v(-15, 90.23) * mm, "end": v(-25, 90.23) * mm});
            skLineSegment(sketch, "E521.MirrorCS", {"start": v(-15, 84.23) * mm, "end": v(-15, 90.23) * mm});
            skLineSegment(sketch, "E522.MirrorCS", {"start": v(15, 84.23) * mm, "end": v(5, 84.23) * mm, "construction": true});
            skLineSegment(sketch, "E523.MirrorCS", {"start": v(35, 84.23) * mm, "end": v(45, 84.23) * mm});
            skLineSegment(sketch, "E524.MirrorCS", {"start": v(15, 84.23) * mm, "end": v(25, 84.23) * mm});
            skLineSegment(sketch, "E525.MirrorCS", {"start": v(0, 84.23) * mm, "end": v(45, 84.23) * mm, "construction": true});
            skLineSegment(sketch, "E526.MirrorCS", {"start": v(45, 84.23) * mm, "end": v(45, 90.23) * mm});
            skLineSegment(sketch, "E527.MirrorCS", {"start": v(45, 90.23) * mm, "end": v(35, 90.23) * mm});
            skLineSegment(sketch, "E528.MirrorCS", {"start": v(35, 90.23) * mm, "end": v(35, 84.23) * mm});
            skLineSegment(sketch, "E529.MirrorCS", {"start": v(35, 84.23) * mm, "end": v(25, 84.23) * mm, "construction": true});
            skLineSegment(sketch, "E530.MirrorCS", {"start": v(25, 84.23) * mm, "end": v(25, 90.23) * mm});
            skLineSegment(sketch, "E531.MirrorCS", {"start": v(25, 90.23) * mm, "end": v(15, 90.23) * mm});
            skLineSegment(sketch, "E532.MirrorCS", {"start": v(15, 90.23) * mm, "end": v(15, 84.23) * mm});
            skLineSegment(sketch, "E533.MirrorCS", {"start": v(-5, 84.23) * mm, "end": v(5, 84.23) * mm});
            skLineSegment(sketch, "E534.MirrorCS", {"start": v(-5, 90.23) * mm, "end": v(-5, 84.23) * mm});
            skLineSegment(sketch, "E535.MirrorCS", {"start": v(5, 90.23) * mm, "end": v(-5, 90.23) * mm});
            skLineSegment(sketch, "E536.MirrorCS", {"start": v(5, 84.23) * mm, "end": v(5, 90.23) * mm});
            skSolve(sketch);
        }
        {
            var Q0;
            Q0 = qSketchRegion(id + "F0", true);
            var Q1;
            Q1 = qConstructionFilter(qBodyType(qCreatedBy(id + "F0" ,EDGE), BodyType.WIRE), ConstructionObject.NO);
            extrude(context, id + "F1", {"entities" : qUnion([Q0]), "surfaceEntities" : qUnion([Q1]), "endBound" : BoundingType.SYMMETRIC, "depth" : 3 * mm});
        }
    });
